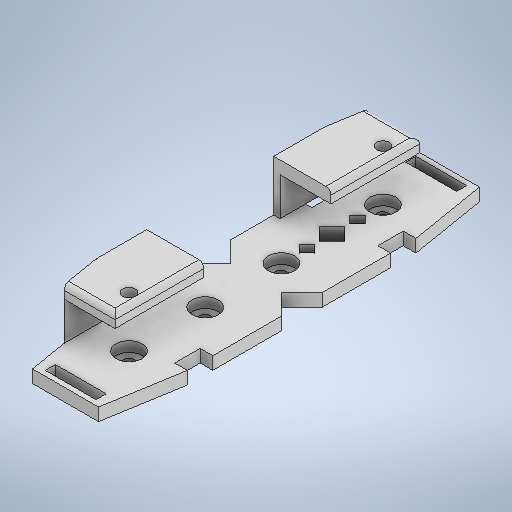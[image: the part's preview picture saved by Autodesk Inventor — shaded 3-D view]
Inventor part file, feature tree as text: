
AUTODESK INVENTOR PART (.ipt)
format: ipt  version: 2025.2 (Build 292293000, 293)  size: 411,136 bytes
history: native  units: mm
features: extrude x7, sketch x6, fillet x1
ambient origin geometry x8: Origin, YZ Plane, XZ Plane, XY Plane, X Axis, Y Axis, Z Axis, Center Point
bodies: Solid1 (feature_tree)
feature tree (14):
  sketch  "Sketch1"  dims[d2=10.2mm d3=25.0mm]
  extrude  "Extrusion1"  Depth=25.0mm
  extrude  "Extrusion2"  Depth=30.0mm
  extrude  "Extrusion3"  Depth=30.0mm
  extrude  "Extrusion4"  Depth=40.0mm
  extrude  "Extrusion5"  Depth=5.0mm
  extrude  "Extrusion6"  Depth=10.0mm
  fillet  "Fillet1"  Radius=5.0mm
  extrude  "Extrusion7"  Depth=5.0mm
  sketch  "Sketch2"  dims[d4=10.2mm d5=30.0mm]
  sketch  "Sketch3"  dims[d6=10.2mm d7=30.0mm]
  sketch  "Sketch4"  dims[d8=10.2mm d9=40.0mm]
  sketch  "Sketch5"  dims[d10=25.0mm d12=5.0mm]
  sketch  "Sketch6"  dims[d13=10.0mm d15=10.0mm d17=5.0mm d19=5.0mm d20=5.0mm d21=0.0mm d22=4.5mm d23=4.5mm d24=4.5mm d25=4.5mm d26=1.0mm d27=0.0mm d38=3.0mm d39=2.0mm d41=2.0mm d42=4.0mm d44=2.0mm d45=3.0mm d46=4.0mm d50=8.0mm d51=8.0mm d52=15.0mm d53=20.0mm d54=0.0mm d55=20.0mm d56=0.0mm d57=20.0mm d58=0.0mm d59=20.0mm d60=0.0mm d61=2.0mm d62=5.0mm d63=5.0mm d64=20.0mm d65=0.0mm]
